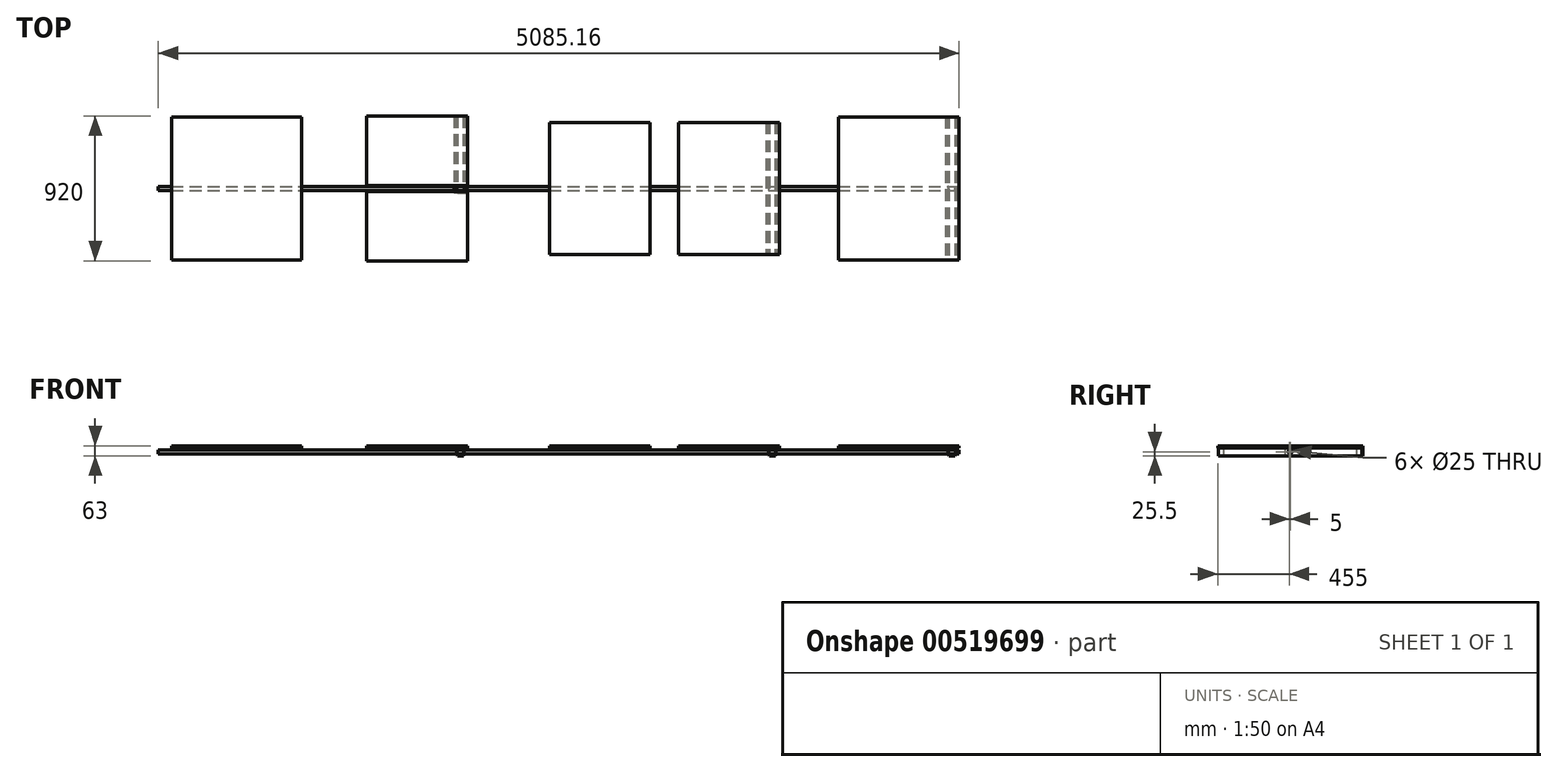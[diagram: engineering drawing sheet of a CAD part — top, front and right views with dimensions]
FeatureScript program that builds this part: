
annotation { "Feature Type Name" : "Feature", "Feature Type Description" : "" }
export const myFeature = defineFeature(function(context is Context, id is Id, definition is map)
    precondition{}
    {
        {
            var Q0;
            Q0=qCreatedBy(makeId("Top.planeOp"),FACE);
            var sketch = newSketch(context, id + "F0", { "sketchPlane" : qUnion([Q0])});
            skLineSegment(sketch, "E0.bottom", {"start": v(-1865.43, 455.05) * mm, "end": v(-2691.93, 455.05) * mm});
            skLineSegment(sketch, "E0.top", {"start": v(-1865.43, -455.05) * mm, "end": v(-2691.93, -455.05) * mm});
            skLineSegment(sketch, "E0.left", {"start": v(-1865.43, 455.05) * mm, "end": v(-1865.43, -455.05) * mm});
            skLineSegment(sketch, "E0.right", {"start": v(-2691.93, 455.05) * mm, "end": v(-2691.93, -455.05) * mm});
            skPoint(sketch, "E0.middle", {"position": v(-2278.68, 0) * mm});
            skLineSegment(sketch, "E1", {"start": v(3394.25, 0) * mm, "end": v(-3825.46, 0) * mm, "construction": true});
            skLineSegment(sketch, "E2", {"start": v(-2691.93, -435.05) * mm, "end": v(-1865.43, -435.05) * mm, "construction": true});
            skLineSegment(sketch, "E3", {"start": v(-2671.93, 455.05) * mm, "end": v(-2671.93, -455.05) * mm, "construction": true});
            skLineSegment(sketch, "E4.0.1.0", {"start": v(-2691.93, -310.75) * mm, "end": v(-1865.43, -310.75) * mm, "construction": true});
            skLineSegment(sketch, "E4.0.2.0", {"start": v(-2691.93, -186.45) * mm, "end": v(-1865.43, -186.45) * mm, "construction": true});
            skLineSegment(sketch, "E4.0.3.0", {"start": v(-2691.93, -62.15) * mm, "end": v(-1865.43, -62.15) * mm, "construction": true});
            skLineSegment(sketch, "E4.0.4.0", {"start": v(-2691.93, 62.15) * mm, "end": v(-1865.43, 62.15) * mm, "construction": true});
            skLineSegment(sketch, "E4.0.5.0", {"start": v(-2691.93, 186.45) * mm, "end": v(-1865.43, 186.45) * mm, "construction": true});
            skLineSegment(sketch, "E4.0.6.0", {"start": v(-2691.93, 310.75) * mm, "end": v(-1865.43, 310.75) * mm, "construction": true});
            skLineSegment(sketch, "E4.0.7.0", {"start": v(-2691.93, 435.05) * mm, "end": v(-1865.43, 435.05) * mm, "construction": true});
            skLineSegment(sketch, "E4.direction1", {"start": v(-2691.93, -435.05) * mm, "end": v(-2691.93, -435.05) * mm});
            skLineSegment(sketch, "E4.direction2", {"start": v(-2691.93, -435.05) * mm, "end": v(-2691.93, -310.75) * mm, "construction": true});
            skLineSegment(sketch, "E5.1.0.0", {"start": v(-2611.43, 455.05) * mm, "end": v(-2611.43, -455.05) * mm, "construction": true});
            skLineSegment(sketch, "E5.2.0.0", {"start": v(-2550.93, 455.05) * mm, "end": v(-2550.93, -455.05) * mm, "construction": true});
            skLineSegment(sketch, "E5.3.0.0", {"start": v(-2490.43, 455.05) * mm, "end": v(-2490.43, -455.05) * mm, "construction": true});
            skLineSegment(sketch, "E5.4.0.0", {"start": v(-2429.93, 455.05) * mm, "end": v(-2429.93, -455.05) * mm, "construction": true});
            skLineSegment(sketch, "E5.5.0.0", {"start": v(-2369.43, 455.05) * mm, "end": v(-2369.43, -455.05) * mm, "construction": true});
            skLineSegment(sketch, "E5.6.0.0", {"start": v(-2308.93, 455.05) * mm, "end": v(-2308.93, -455.05) * mm, "construction": true});
            skLineSegment(sketch, "E5.7.0.0", {"start": v(-2248.43, 455.05) * mm, "end": v(-2248.43, -455.05) * mm, "construction": true});
            skLineSegment(sketch, "E5.8.0.0", {"start": v(-2187.93, 455.05) * mm, "end": v(-2187.93, -455.05) * mm, "construction": true});
            skLineSegment(sketch, "E5.9.0.0", {"start": v(-2127.43, 455.05) * mm, "end": v(-2127.43, -455.05) * mm, "construction": true});
            skLineSegment(sketch, "E5.10.0.0", {"start": v(-2066.93, 455.05) * mm, "end": v(-2066.93, -455.05) * mm, "construction": true});
            skLineSegment(sketch, "E5.11.0.0", {"start": v(-2006.43, 455.05) * mm, "end": v(-2006.43, -455.05) * mm, "construction": true});
            skLineSegment(sketch, "E5.12.0.0", {"start": v(-1945.93, 455.05) * mm, "end": v(-1945.93, -455.05) * mm, "construction": true});
            skLineSegment(sketch, "E5.13.0.0", {"start": v(-1885.43, 455.05) * mm, "end": v(-1885.43, -455.05) * mm, "construction": true});
            skLineSegment(sketch, "E5.direction1", {"start": v(-2671.93, -455.05) * mm, "end": v(-2611.43, -455.05) * mm, "construction": true});
            skLineSegment(sketch, "E6", {"start": v(-2611.43, -310.75) * mm, "end": v(-2611.43, -435.05) * mm, "construction": true});
            skLineSegment(sketch, "E7", {"start": v(-2611.43, -310.75) * mm, "end": v(-2671.93, -310.75) * mm, "construction": true});
            skLineSegment(sketch, "E8.bottom", {"start": v(2308.9, 455.05) * mm, "end": v(1542.9, 455.05) * mm});
            skLineSegment(sketch, "E8.top", {"start": v(2308.9, -455.05) * mm, "end": v(1542.9, -455.05) * mm});
            skLineSegment(sketch, "E8.left", {"start": v(2308.9, 455.05) * mm, "end": v(2308.9, -455.05) * mm});
            skLineSegment(sketch, "E8.right", {"start": v(1542.9, 455.05) * mm, "end": v(1542.9, -455.05) * mm});
            skPoint(sketch, "E8.middle", {"position": v(1925.9, 0) * mm});
            skLineSegment(sketch, "E9", {"start": v(1542.9, -435.05) * mm, "end": v(2308.9, -435.05) * mm, "construction": true});
            skLineSegment(sketch, "E10", {"start": v(1562.9, 455.05) * mm, "end": v(1562.9, -455.05) * mm, "construction": true});
            skLineSegment(sketch, "E11.0.1.0", {"start": v(1542.9, -310.75) * mm, "end": v(2308.9, -310.75) * mm, "construction": true});
            skLineSegment(sketch, "E11.0.2.0", {"start": v(1542.9, -186.45) * mm, "end": v(2308.9, -186.45) * mm, "construction": true});
            skLineSegment(sketch, "E11.0.3.0", {"start": v(1542.9, -62.15) * mm, "end": v(2308.9, -62.15) * mm, "construction": true});
            skLineSegment(sketch, "E11.0.4.0", {"start": v(1542.9, 62.15) * mm, "end": v(2308.9, 62.15) * mm, "construction": true});
            skLineSegment(sketch, "E11.0.5.0", {"start": v(1542.9, 186.45) * mm, "end": v(2308.9, 186.45) * mm, "construction": true});
            skLineSegment(sketch, "E11.0.6.0", {"start": v(1542.9, 310.75) * mm, "end": v(2308.9, 310.75) * mm, "construction": true});
            skLineSegment(sketch, "E11.0.7.0", {"start": v(1542.9, 435.05) * mm, "end": v(2308.9, 435.05) * mm, "construction": true});
            skLineSegment(sketch, "E11.direction1", {"start": v(1542.9, -435.05) * mm, "end": v(1542.9, -435.05) * mm});
            skLineSegment(sketch, "E11.direction2", {"start": v(1542.9, -435.05) * mm, "end": v(1542.9, -310.75) * mm, "construction": true});
            skLineSegment(sketch, "E12.1.0.0", {"start": v(1623.4, 455.05) * mm, "end": v(1623.4, -455.05) * mm, "construction": true});
            skLineSegment(sketch, "E12.2.0.0", {"start": v(1683.9, 455.05) * mm, "end": v(1683.9, -455.05) * mm, "construction": true});
            skLineSegment(sketch, "E12.3.0.0", {"start": v(1744.4, 455.05) * mm, "end": v(1744.4, -455.05) * mm, "construction": true});
            skLineSegment(sketch, "E12.4.0.0", {"start": v(1804.9, 455.05) * mm, "end": v(1804.9, -455.05) * mm, "construction": true});
            skLineSegment(sketch, "E12.5.0.0", {"start": v(1865.4, 455.05) * mm, "end": v(1865.4, -455.05) * mm, "construction": true});
            skLineSegment(sketch, "E12.6.0.0", {"start": v(1925.9, 455.05) * mm, "end": v(1925.9, -455.05) * mm, "construction": true});
            skLineSegment(sketch, "E12.7.0.0", {"start": v(1986.4, 455.05) * mm, "end": v(1986.4, -455.05) * mm, "construction": true});
            skLineSegment(sketch, "E12.8.0.0", {"start": v(2046.9, 455.05) * mm, "end": v(2046.9, -455.05) * mm, "construction": true});
            skLineSegment(sketch, "E12.9.0.0", {"start": v(2107.4, 455.05) * mm, "end": v(2107.4, -455.05) * mm, "construction": true});
            skLineSegment(sketch, "E12.10.0.0", {"start": v(2167.9, 455.05) * mm, "end": v(2167.9, -455.05) * mm, "construction": true});
            skLineSegment(sketch, "E12.11.0.0", {"start": v(2228.4, 455.05) * mm, "end": v(2228.4, -455.05) * mm, "construction": true});
            skLineSegment(sketch, "E12.12.0.0", {"start": v(2288.9, 455.05) * mm, "end": v(2288.9, -455.05) * mm, "construction": true});
            skLineSegment(sketch, "E12.direction1", {"start": v(1562.9, -455.05) * mm, "end": v(1623.4, -455.05) * mm, "construction": true});
            skLineSegment(sketch, "E13", {"start": v(1623.4, -310.75) * mm, "end": v(1623.4, -435.05) * mm, "construction": true});
            skLineSegment(sketch, "E14", {"start": v(1623.4, -310.75) * mm, "end": v(1562.9, -310.75) * mm, "construction": true});
            skLineSegment(sketch, "E15.bottom", {"start": v(1167.87, 420) * mm, "end": v(527.87, 420) * mm});
            skLineSegment(sketch, "E15.top", {"start": v(1167.87, -420) * mm, "end": v(527.87, -420) * mm});
            skLineSegment(sketch, "E15.left", {"start": v(1167.87, 420) * mm, "end": v(1167.87, -420) * mm});
            skLineSegment(sketch, "E15.right", {"start": v(527.87, 420) * mm, "end": v(527.87, -420) * mm});
            skLineSegment(sketch, "E16", {"start": v(527.87, -400) * mm, "end": v(1167.87, -400) * mm, "construction": true});
            skLineSegment(sketch, "E17", {"start": v(547.87, 420) * mm, "end": v(547.87, -420) * mm, "construction": true});
            skLineSegment(sketch, "E18.0.1.0", {"start": v(527.87, -320) * mm, "end": v(1167.87, -320) * mm, "construction": true});
            skLineSegment(sketch, "E18.0.2.0", {"start": v(527.87, -240) * mm, "end": v(1167.87, -240) * mm, "construction": true});
            skLineSegment(sketch, "E18.0.3.0", {"start": v(527.87, -160) * mm, "end": v(1167.87, -160) * mm, "construction": true});
            skLineSegment(sketch, "E18.0.4.0", {"start": v(527.87, -80) * mm, "end": v(1167.87, -80) * mm, "construction": true});
            skLineSegment(sketch, "E18.0.5.0", {"start": v(527.87, 0) * mm, "end": v(1167.87, 0) * mm, "construction": true});
            skLineSegment(sketch, "E18.0.6.0", {"start": v(527.87, 80) * mm, "end": v(1167.87, 80) * mm, "construction": true});
            skLineSegment(sketch, "E18.0.7.0", {"start": v(527.87, 160) * mm, "end": v(1167.87, 160) * mm, "construction": true});
            skLineSegment(sketch, "E18.direction1", {"start": v(527.87, -400) * mm, "end": v(527.87, -400) * mm});
            skLineSegment(sketch, "E18.direction2", {"start": v(527.87, -400) * mm, "end": v(527.87, -320) * mm, "construction": true});
            skLineSegment(sketch, "E19.1.0.0", {"start": v(587.87, 420) * mm, "end": v(587.87, -420) * mm, "construction": true});
            skLineSegment(sketch, "E19.2.0.0", {"start": v(627.87, 420) * mm, "end": v(627.87, -420) * mm, "construction": true});
            skLineSegment(sketch, "E19.3.0.0", {"start": v(667.87, 420) * mm, "end": v(667.87, -420) * mm, "construction": true});
            skLineSegment(sketch, "E19.4.0.0", {"start": v(707.87, 420) * mm, "end": v(707.87, -420) * mm, "construction": true});
            skLineSegment(sketch, "E19.5.0.0", {"start": v(747.87, 420) * mm, "end": v(747.87, -420) * mm, "construction": true});
            skLineSegment(sketch, "E19.6.0.0", {"start": v(787.87, 420) * mm, "end": v(787.87, -420) * mm, "construction": true});
            skLineSegment(sketch, "E19.7.0.0", {"start": v(827.87, 420) * mm, "end": v(827.87, -420) * mm, "construction": true});
            skLineSegment(sketch, "E19.8.0.0", {"start": v(867.87, 420) * mm, "end": v(867.87, -420) * mm, "construction": true});
            skLineSegment(sketch, "E19.9.0.0", {"start": v(907.87, 420) * mm, "end": v(907.87, -420) * mm, "construction": true});
            skLineSegment(sketch, "E19.10.0.0", {"start": v(947.87, 420) * mm, "end": v(947.87, -420) * mm, "construction": true});
            skLineSegment(sketch, "E19.11.0.0", {"start": v(987.87, 420) * mm, "end": v(987.87, -420) * mm, "construction": true});
            skLineSegment(sketch, "E19.12.0.0", {"start": v(1027.87, 420) * mm, "end": v(1027.87, -420) * mm, "construction": true});
            skLineSegment(sketch, "E19.13.0.0", {"start": v(1067.87, 420) * mm, "end": v(1067.87, -420) * mm, "construction": true});
            skLineSegment(sketch, "E19.direction1", {"start": v(547.87, -420) * mm, "end": v(587.87, -420) * mm, "construction": true});
            skLineSegment(sketch, "E20", {"start": v(587.87, -320) * mm, "end": v(587.87, -400) * mm, "construction": true});
            skLineSegment(sketch, "E21.0.14.0", {"start": v(1107.87, 420) * mm, "end": v(1107.87, -420) * mm, "construction": true});
            skLineSegment(sketch, "E21.0.15.0", {"start": v(1147.87, 420) * mm, "end": v(1147.87, -420) * mm, "construction": true});
            skLineSegment(sketch, "E22.0.0.8", {"start": v(527.87, 240) * mm, "end": v(1167.87, 240) * mm, "construction": true});
            skLineSegment(sketch, "E22.0.0.9", {"start": v(527.87, 320) * mm, "end": v(1167.87, 320) * mm, "construction": true});
            skLineSegment(sketch, "E22.0.0.10", {"start": v(527.87, 400) * mm, "end": v(1167.87, 400) * mm, "construction": true});
            skLineSegment(sketch, "E23.bottom", {"start": v(347.86, 420) * mm, "end": v(-292.14, 420) * mm});
            skLineSegment(sketch, "E23.top", {"start": v(347.86, -420) * mm, "end": v(-292.14, -420) * mm});
            skLineSegment(sketch, "E23.left", {"start": v(347.86, 420) * mm, "end": v(347.86, -420) * mm});
            skLineSegment(sketch, "E23.right", {"start": v(-292.14, 420) * mm, "end": v(-292.14, -420) * mm});
            skPoint(sketch, "E23.middle", {"position": v(27.86, 0) * mm});
            skLineSegment(sketch, "E24", {"start": v(-292.14, -400) * mm, "end": v(347.86, -400) * mm, "construction": true});
            skLineSegment(sketch, "E25", {"start": v(-272.14, 420) * mm, "end": v(-272.14, -420) * mm, "construction": true});
            skLineSegment(sketch, "E26.0.1.0", {"start": v(-292.14, -320) * mm, "end": v(347.86, -320) * mm, "construction": true});
            skLineSegment(sketch, "E26.0.2.0", {"start": v(-292.14, -240) * mm, "end": v(347.86, -240) * mm, "construction": true});
            skLineSegment(sketch, "E26.0.3.0", {"start": v(-292.14, -160) * mm, "end": v(347.86, -160) * mm, "construction": true});
            skLineSegment(sketch, "E26.0.4.0", {"start": v(-292.14, -80) * mm, "end": v(347.86, -80) * mm, "construction": true});
            skLineSegment(sketch, "E26.0.5.0", {"start": v(-292.14, 0) * mm, "end": v(347.86, 0) * mm, "construction": true});
            skLineSegment(sketch, "E26.0.6.0", {"start": v(-292.14, 80) * mm, "end": v(347.86, 80) * mm, "construction": true});
            skLineSegment(sketch, "E26.0.7.0", {"start": v(-292.14, 160) * mm, "end": v(347.86, 160) * mm, "construction": true});
            skLineSegment(sketch, "E26.direction1", {"start": v(-292.14, -400) * mm, "end": v(-292.14, -400) * mm});
            skLineSegment(sketch, "E26.direction2", {"start": v(-292.14, -400) * mm, "end": v(-292.14, -320) * mm, "construction": true});
            skLineSegment(sketch, "E27.1.0.0", {"start": v(-232.14, 420) * mm, "end": v(-232.14, -420) * mm, "construction": true});
            skLineSegment(sketch, "E27.2.0.0", {"start": v(-192.14, 420) * mm, "end": v(-192.14, -420) * mm, "construction": true});
            skLineSegment(sketch, "E27.3.0.0", {"start": v(-152.14, 420) * mm, "end": v(-152.14, -420) * mm, "construction": true});
            skLineSegment(sketch, "E27.4.0.0", {"start": v(-112.14, 420) * mm, "end": v(-112.14, -420) * mm, "construction": true});
            skLineSegment(sketch, "E27.5.0.0", {"start": v(-72.14, 420) * mm, "end": v(-72.14, -420) * mm, "construction": true});
            skLineSegment(sketch, "E27.6.0.0", {"start": v(-32.14, 420) * mm, "end": v(-32.14, -420) * mm, "construction": true});
            skLineSegment(sketch, "E27.7.0.0", {"start": v(7.86, 420) * mm, "end": v(7.86, -420) * mm, "construction": true});
            skLineSegment(sketch, "E27.8.0.0", {"start": v(47.86, 420) * mm, "end": v(47.86, -420) * mm, "construction": true});
            skLineSegment(sketch, "E27.9.0.0", {"start": v(87.86, 420) * mm, "end": v(87.86, -420) * mm, "construction": true});
            skLineSegment(sketch, "E27.10.0.0", {"start": v(127.86, 420) * mm, "end": v(127.86, -420) * mm, "construction": true});
            skLineSegment(sketch, "E27.11.0.0", {"start": v(167.86, 420) * mm, "end": v(167.86, -420) * mm, "construction": true});
            skLineSegment(sketch, "E27.12.0.0", {"start": v(207.86, 420) * mm, "end": v(207.86, -420) * mm, "construction": true});
            skLineSegment(sketch, "E27.13.0.0", {"start": v(247.86, 420) * mm, "end": v(247.86, -420) * mm, "construction": true});
            skLineSegment(sketch, "E27.direction1", {"start": v(-272.14, -420) * mm, "end": v(-232.14, -420) * mm, "construction": true});
            skLineSegment(sketch, "E28", {"start": v(-232.14, -320) * mm, "end": v(-232.14, -400) * mm, "construction": true});
            skLineSegment(sketch, "E29.0.14.0", {"start": v(287.86, 420) * mm, "end": v(287.86, -420) * mm, "construction": true});
            skLineSegment(sketch, "E29.0.15.0", {"start": v(327.86, 420) * mm, "end": v(327.86, -420) * mm, "construction": true});
            skLineSegment(sketch, "E30.0.0.8", {"start": v(-292.14, 240) * mm, "end": v(347.86, 240) * mm, "construction": true});
            skLineSegment(sketch, "E30.0.0.9", {"start": v(-292.14, 320) * mm, "end": v(347.86, 320) * mm, "construction": true});
            skLineSegment(sketch, "E30.0.0.10", {"start": v(-292.14, 400) * mm, "end": v(347.86, 400) * mm, "construction": true});
            skLineSegment(sketch, "E31.bottom", {"start": v(-813.38, 460) * mm, "end": v(-1453.38, 460) * mm});
            skLineSegment(sketch, "E31.top", {"start": v(-813.38, 20) * mm, "end": v(-1453.38, 20) * mm});
            skLineSegment(sketch, "E31.left", {"start": v(-813.38, 460) * mm, "end": v(-813.38, 20) * mm});
            skLineSegment(sketch, "E31.right", {"start": v(-1453.38, 460) * mm, "end": v(-1453.38, 20) * mm});
            skPoint(sketch, "E31.middle", {"position": v(-1133.38, 240) * mm});
            skLineSegment(sketch, "E32", {"start": v(-1453.38, 40) * mm, "end": v(-813.38, 40) * mm, "construction": true});
            skLineSegment(sketch, "E33", {"start": v(-1433.38, 460) * mm, "end": v(-1433.38, 20) * mm, "construction": true});
            skLineSegment(sketch, "E34.0.1.0", {"start": v(-1453.38, 120) * mm, "end": v(-813.38, 120) * mm, "construction": true});
            skLineSegment(sketch, "E34.0.2.0", {"start": v(-1453.38, 200) * mm, "end": v(-813.38, 200) * mm, "construction": true});
            skLineSegment(sketch, "E34.0.3.0", {"start": v(-1453.38, 280) * mm, "end": v(-813.38, 280) * mm, "construction": true});
            skLineSegment(sketch, "E34.0.4.0", {"start": v(-1453.38, 360) * mm, "end": v(-813.38, 360) * mm, "construction": true});
            skLineSegment(sketch, "E34.0.5.0", {"start": v(-1453.38, 440) * mm, "end": v(-813.38, 440) * mm, "construction": true});
            skLineSegment(sketch, "E34.direction1", {"start": v(-1453.38, 40) * mm, "end": v(-1453.38, 40) * mm});
            skLineSegment(sketch, "E34.direction2", {"start": v(-1453.38, 40) * mm, "end": v(-1453.38, 120) * mm, "construction": true});
            skLineSegment(sketch, "E35.1.0.0", {"start": v(-1393.38, 460) * mm, "end": v(-1393.38, 20) * mm, "construction": true});
            skLineSegment(sketch, "E35.2.0.0", {"start": v(-1353.38, 460) * mm, "end": v(-1353.38, 20) * mm, "construction": true});
            skLineSegment(sketch, "E35.3.0.0", {"start": v(-1313.38, 460) * mm, "end": v(-1313.38, 20) * mm, "construction": true});
            skLineSegment(sketch, "E35.4.0.0", {"start": v(-1273.38, 460) * mm, "end": v(-1273.38, 20) * mm, "construction": true});
            skLineSegment(sketch, "E35.5.0.0", {"start": v(-1233.38, 460) * mm, "end": v(-1233.38, 20) * mm, "construction": true});
            skLineSegment(sketch, "E35.6.0.0", {"start": v(-1193.38, 460) * mm, "end": v(-1193.38, 20) * mm, "construction": true});
            skLineSegment(sketch, "E35.7.0.0", {"start": v(-1153.38, 460) * mm, "end": v(-1153.38, 20) * mm, "construction": true});
            skLineSegment(sketch, "E35.8.0.0", {"start": v(-1113.38, 460) * mm, "end": v(-1113.38, 20) * mm, "construction": true});
            skLineSegment(sketch, "E35.9.0.0", {"start": v(-1073.38, 460) * mm, "end": v(-1073.38, 20) * mm, "construction": true});
            skLineSegment(sketch, "E35.10.0.0", {"start": v(-1033.38, 460) * mm, "end": v(-1033.38, 20) * mm, "construction": true});
            skLineSegment(sketch, "E35.11.0.0", {"start": v(-993.38, 460) * mm, "end": v(-993.38, 20) * mm, "construction": true});
            skLineSegment(sketch, "E35.12.0.0", {"start": v(-953.38, 460) * mm, "end": v(-953.38, 20) * mm, "construction": true});
            skLineSegment(sketch, "E35.13.0.0", {"start": v(-913.38, 460) * mm, "end": v(-913.38, 20) * mm, "construction": true});
            skLineSegment(sketch, "E35.direction1", {"start": v(-1433.38, 20) * mm, "end": v(-1393.38, 20) * mm, "construction": true});
            skLineSegment(sketch, "E36", {"start": v(-1393.38, 120) * mm, "end": v(-1393.38, 40) * mm, "construction": true});
            skLineSegment(sketch, "E37", {"start": v(-1393.38, 120) * mm, "end": v(-1433.38, 120) * mm, "construction": true});
            skLineSegment(sketch, "E38.0.14.0", {"start": v(-873.38, 460) * mm, "end": v(-873.38, 20) * mm, "construction": true});
            skLineSegment(sketch, "E38.0.15.0", {"start": v(-833.38, 460) * mm, "end": v(-833.38, 20) * mm, "construction": true});
            skLineSegment(sketch, "E39", {"start": v(-1133.38, 240) * mm, "end": v(-1133.38, 0) * mm, "construction": true});
            skLineSegment(sketch, "E40.MirrorCS", {"start": v(-1433.38, -20) * mm, "end": v(-1393.38, -20) * mm, "construction": true});
            skLineSegment(sketch, "E41.MirrorCS", {"start": v(-1393.38, -120) * mm, "end": v(-1433.38, -120) * mm, "construction": true});
            skLineSegment(sketch, "E42.MirrorCS", {"start": v(-1453.38, -40) * mm, "end": v(-1453.38, -120) * mm, "construction": true});
            skLineSegment(sketch, "E43.MirrorCS", {"start": v(-813.38, -460) * mm, "end": v(-813.38, -20) * mm});
            skLineSegment(sketch, "E44.MirrorCS", {"start": v(-1453.38, -40) * mm, "end": v(-813.38, -40) * mm, "construction": true});
            skLineSegment(sketch, "E45.MirrorCS", {"start": v(-1453.38, -460) * mm, "end": v(-1453.38, -20) * mm});
            skLineSegment(sketch, "E46.MirrorCS", {"start": v(-1453.38, -440) * mm, "end": v(-813.38, -440) * mm, "construction": true});
            skLineSegment(sketch, "E47.MirrorCS", {"start": v(-1393.38, -120) * mm, "end": v(-1393.38, -40) * mm, "construction": true});
            skLineSegment(sketch, "E48.MirrorCS", {"start": v(-813.38, -460) * mm, "end": v(-1453.38, -460) * mm});
            skLineSegment(sketch, "E49.MirrorCS", {"start": v(-833.38, -460) * mm, "end": v(-833.38, -20) * mm, "construction": true});
            skLineSegment(sketch, "E50.MirrorCS", {"start": v(-1433.38, -460) * mm, "end": v(-1433.38, -20) * mm, "construction": true});
            skLineSegment(sketch, "E51.MirrorCS", {"start": v(-813.38, -20) * mm, "end": v(-1453.38, -20) * mm});
            skLineSegment(sketch, "E52.MirrorCS", {"start": v(-1453.38, -280) * mm, "end": v(-813.38, -280) * mm, "construction": true});
            skLineSegment(sketch, "E53.MirrorCS", {"start": v(-1273.38, -460) * mm, "end": v(-1273.38, -20) * mm, "construction": true});
            skLineSegment(sketch, "E54.MirrorCS", {"start": v(-1113.38, -460) * mm, "end": v(-1113.38, -20) * mm, "construction": true});
            skLineSegment(sketch, "E55.MirrorCS", {"start": v(-1453.38, -360) * mm, "end": v(-813.38, -360) * mm, "construction": true});
            skLineSegment(sketch, "E56.MirrorCS", {"start": v(-1153.38, -460) * mm, "end": v(-1153.38, -20) * mm, "construction": true});
            skLineSegment(sketch, "E57.MirrorCS", {"start": v(-1453.38, -200) * mm, "end": v(-813.38, -200) * mm, "construction": true});
            skLineSegment(sketch, "E58.MirrorCS", {"start": v(-953.38, -460) * mm, "end": v(-953.38, -20) * mm, "construction": true});
            skLineSegment(sketch, "E59.MirrorCS", {"start": v(-1453.38, -120) * mm, "end": v(-813.38, -120) * mm, "construction": true});
            skLineSegment(sketch, "E60.MirrorCS", {"start": v(-993.38, -460) * mm, "end": v(-993.38, -20) * mm, "construction": true});
            skLineSegment(sketch, "E61.MirrorCS", {"start": v(-1133.38, -240) * mm, "end": v(-1133.38, 0) * mm, "construction": true});
            skLineSegment(sketch, "E62.MirrorCS", {"start": v(-1313.38, -460) * mm, "end": v(-1313.38, -20) * mm, "construction": true});
            skLineSegment(sketch, "E63.MirrorCS", {"start": v(-1353.38, -460) * mm, "end": v(-1353.38, -20) * mm, "construction": true});
            skLineSegment(sketch, "E64.MirrorCS", {"start": v(-1033.38, -460) * mm, "end": v(-1033.38, -20) * mm, "construction": true});
            skPoint(sketch, "E65.MirrorP", {"position": v(-1133.38, -240) * mm});
            skLineSegment(sketch, "E66.MirrorCS", {"start": v(-873.38, -460) * mm, "end": v(-873.38, -20) * mm, "construction": true});
            skLineSegment(sketch, "E67.MirrorCS", {"start": v(-1233.38, -460) * mm, "end": v(-1233.38, -20) * mm, "construction": true});
            skLineSegment(sketch, "E68.MirrorCS", {"start": v(-1393.38, -460) * mm, "end": v(-1393.38, -20) * mm, "construction": true});
            skLineSegment(sketch, "E69.MirrorCS", {"start": v(-1073.38, -460) * mm, "end": v(-1073.38, -20) * mm, "construction": true});
            skLineSegment(sketch, "E70.MirrorCS", {"start": v(-913.38, -460) * mm, "end": v(-913.38, -20) * mm, "construction": true});
            skLineSegment(sketch, "E71.MirrorCS", {"start": v(-1193.38, -460) * mm, "end": v(-1193.38, -20) * mm, "construction": true});
            skSolve(sketch);
        }
        {
            var Q0;
            Q0=makeQuery(id+"F0.imprint","IMPRINT",FACE,{"disambiguationData":[TD([[makeQuery(id+"F0.imprint","IMPRINT",EDGE,{"derivedFrom":sQuery(id+"F0.wireOp",EDGE,"E0.bottom")}),1.0]])]});
            extrude(context, id + "F1", {"entities" : qUnion([Q0]), "depth" : 12 * mm, "offsetDistance" : 25 * mm});
        }
        {
            var Q0;
            Q0=makeQuery(id+"F0.imprint","IMPRINT",FACE,{"disambiguationData":[TD([[makeQuery(id+"F0.imprint","IMPRINT",EDGE,{"derivedFrom":sQuery(id+"F0.wireOp",EDGE,"E23.bottom")}),1.0]])]});
            extrude(context, id + "F2", {"entities" : qUnion([Q0]), "depth" : 12 * mm, "offsetDistance" : 25 * mm});
        }
        {
            var Q0;
            Q0=makeQuery(id+"F0.imprint","IMPRINT",FACE,{"disambiguationData":[TD([[makeQuery(id+"F0.imprint","IMPRINT",EDGE,{"derivedFrom":sQuery(id+"F0.wireOp",EDGE,"E15.bottom")}),1.0]])]});
            extrude(context, id + "F3", {"entities" : qUnion([Q0]), "depth" : 12 * mm, "offsetDistance" : 25 * mm});
        }
        {
            var Q0;
            Q0=makeQuery(id+"F0.imprint","IMPRINT",FACE,{"disambiguationData":[TD([[makeQuery(id+"F0.imprint","IMPRINT",EDGE,{"derivedFrom":sQuery(id+"F0.wireOp",EDGE,"E8.bottom")}),1.0]])]});
            extrude(context, id + "F4", {"entities" : qUnion([Q0]), "depth" : 12 * mm, "offsetDistance" : 25 * mm});
        }
        {
            var Q0;
            Q0=makeQuery(id+"F4.opExtrude","SWEPT_FACE",FACE,{"disambiguationData":[OSD([sQuery(id+"F0.wireOp",EDGE,"E8.left")])]});
            var sketch = newSketch(context, id + "F5", { "sketchPlane" : qUnion([Q0])});
            skPoint(sketch, "E72.oppositeSnap0", {"position": v(455.05, 6) * mm});
            skLineSegment(sketch, "E72.bottom", {"start": v(-455.05, 0) * mm, "end": v(455.05, 0) * mm});
            skLineSegment(sketch, "E72.top", {"start": v(-455.05, -51) * mm, "end": v(455.05, -51) * mm});
            skLineSegment(sketch, "E72.left", {"start": v(-455.05, 0) * mm, "end": v(-455.05, -51) * mm});
            skLineSegment(sketch, "E72.right", {"start": v(455.05, 0) * mm, "end": v(455.05, -51) * mm});
            skCircle(sketch, "E73", {"center": v(0, -25.5) * mm, "radius": 12.5 * mm});
            skPoint(sketch, "E73.centerSnap0", {"position": v(0, 0) * mm});
            skPoint(sketch, "E74", {"position": v(-455.05, -25.5) * mm});
            skSolve(sketch);
        }
        {
            var Q0;
            Q0 = qSketchRegion(id + "F5", true);
            extrude(context, id + "F6", {"entities" : qUnion([Q0]), "oppositeDirection" : true, "depth" : 10 * mm, "offsetDistance" : 25 * mm});
        }
        {
            var Q0;
            Q0=makeQuery(id+"F3.opExtrude","SWEPT_FACE",FACE,{"disambiguationData":[OSD([sQuery(id+"F0.wireOp",EDGE,"E15.left")])]});
            var sketch = newSketch(context, id + "F7", { "sketchPlane" : qUnion([Q0])});
            skLineSegment(sketch, "E75.bottom", {"start": v(-420, 0) * mm, "end": v(420, 0) * mm});
            skLineSegment(sketch, "E75.top", {"start": v(-420, -51) * mm, "end": v(420, -51) * mm});
            skLineSegment(sketch, "E75.left", {"start": v(-420, 0) * mm, "end": v(-420, -51) * mm});
            skLineSegment(sketch, "E75.right", {"start": v(420, 0) * mm, "end": v(420, -51) * mm});
            skCircle(sketch, "E76", {"center": v(0, -25.5) * mm, "radius": 12.5 * mm});
            skPoint(sketch, "E76.centerSnap0", {"position": v(0, 0) * mm});
            skPoint(sketch, "E77", {"position": v(-420, -25.5) * mm});
            skSolve(sketch);
        }
        {
            var Q0;
            Q0 = qSketchRegion(id + "F7", true);
            extrude(context, id + "F8", {"entities" : qUnion([Q0]), "oppositeDirection" : true, "depth" : 10 * mm, "offsetDistance" : 25 * mm});
        }
        {
            var Q0;
            Q0=makeQuery(id+"F0.imprint","IMPRINT",FACE,{"disambiguationData":[TD([[makeQuery(id+"F0.imprint","IMPRINT",EDGE,{"derivedFrom":sQuery(id+"F0.wireOp",EDGE,"E31.bottom")}),1.0]])]});
            extrude(context, id + "F9", {"entities" : qUnion([Q0]), "depth" : 12 * mm, "offsetDistance" : 25 * mm});
        }
        {
            var Q0;
            Q0=makeQuery(id+"F0.imprint","IMPRINT",FACE,{"disambiguationData":[TD([[makeQuery(id+"F0.imprint","IMPRINT",EDGE,{"derivedFrom":sQuery(id+"F0.wireOp",EDGE,"E43.MirrorCS")}),1.0]])]});
            extrude(context, id + "F10", {"entities" : qUnion([Q0]), "depth" : 12 * mm, "offsetDistance" : 25 * mm});
        }
        {
            var Q0;
            Q0=makeQuery(id+"F9.opExtrude","SWEPT_FACE",FACE,{"disambiguationData":[OSD([sQuery(id+"F0.wireOp",EDGE,"E31.left")])]});
            var sketch = newSketch(context, id + "F11", { "sketchPlane" : qUnion([Q0])});
            skCircle(sketch, "E78.0", {"center": v(-5, -25.5) * mm, "radius": 12.5 * mm});
            skLineSegment(sketch, "E79.bottom", {"start": v(20, 0) * mm, "end": v(460, 0) * mm});
            skLineSegment(sketch, "E79.top", {"start": v(20, -51) * mm, "end": v(460, -51) * mm});
            skLineSegment(sketch, "E79.left", {"start": v(20, 0) * mm, "end": v(20, -51) * mm});
            skLineSegment(sketch, "E79.right", {"start": v(460, 0) * mm, "end": v(460, -51) * mm});
            skLineSegment(sketch, "E80.bottom", {"start": v(20, 0) * mm, "end": v(-30, 0) * mm});
            skLineSegment(sketch, "E80.top", {"start": v(20, -51) * mm, "end": v(-30, -51) * mm});
            skLineSegment(sketch, "E80.right", {"start": v(-30, 0) * mm, "end": v(-30, -51) * mm});
            skPoint(sketch, "E81.0", {"position": v(-30, 0) * mm});
            skPoint(sketch, "E82", {"position": v(-30, -25.5) * mm});
            skPoint(sketch, "E83", {"position": v(-5, 0) * mm});
            skSolve(sketch);
        }
        {
            var Q0;
            Q0 = qSketchRegion(id + "F11", true);
            extrude(context, id + "F12", {"entities" : qUnion([Q0]), "oppositeDirection" : true, "depth" : 10 * mm, "offsetDistance" : 25 * mm});
        }
        {
            var Q0;
            Q0=makeQuery(id+"F12.opExtrude","SWEPT_FACE",FACE,{"disambiguationData":[OSD([sQuery(id+"F11.wireOp",EDGE,"E80.right")])]});
            var sketch = newSketch(context, id + "F13", { "sketchPlane" : qUnion([Q0])});
            skLineSegment(sketch, "E84", {"start": v(-836.32, -50) * mm, "end": v(-845.14, 0) * mm});
            skPoint(sketch, "E85", {"position": v(-818.38, 0) * mm});
            skPoint(sketch, "E86", {"position": v(-818.38, -51) * mm});
            skLineSegment(sketch, "E87", {"start": v(-818.38, -51) * mm, "end": v(-818.38, 0) * mm, "construction": true});
            skLineSegment(sketch, "E88", {"start": v(-845.14, 0) * mm, "end": v(-860.14, 0) * mm});
            skLineSegment(sketch, "E89.MirrorCS", {"start": v(-791.61, 0) * mm, "end": v(-776.61, 0) * mm});
            skLineSegment(sketch, "E90.MirrorCS", {"start": v(-800.43, -50) * mm, "end": v(-791.61, 0) * mm});
            skLineSegment(sketch, "E91", {"start": v(-836.32, -50) * mm, "end": v(-800.43, -50) * mm});
            skLineSegment(sketch, "E92.0", {"start": v(-845.98, -1) * mm, "end": v(-860.14, -1) * mm});
            skLineSegment(sketch, "E92.1", {"start": v(-790.78, -1) * mm, "end": v(-776.61, -1) * mm});
            skLineSegment(sketch, "E92.2", {"start": v(-799.6, -51) * mm, "end": v(-790.78, -1) * mm});
            skLineSegment(sketch, "E92.3", {"start": v(-837.16, -51) * mm, "end": v(-799.6, -51) * mm});
            skLineSegment(sketch, "E92.4", {"start": v(-837.16, -51) * mm, "end": v(-845.98, -1) * mm});
            skLineSegment(sketch, "E93", {"start": v(-860.14, 0) * mm, "end": v(-860.14, -1) * mm});
            skLineSegment(sketch, "E94", {"start": v(-776.61, 0) * mm, "end": v(-776.61, -1) * mm});
            skSolve(sketch);
        }
        {
            var Q0;
            Q0 = qSketchRegion(id + "F13", true);
            var Q1;
            Q1=makeQuery(id+"F12.opExtrude","SWEPT_FACE",FACE,{"disambiguationData":[OSD([sQuery(id+"F11.wireOp",EDGE,"E79.right")])]});
            extrude(context, id + "F14", {"entities" : qUnion([Q0]), "endBound" : BoundingType.UP_TO_SURFACE, "oppositeDirection" : true, "depth" : 25 * mm, "endBoundEntityFace" : qUnion([Q1]), "offsetDistance" : 25 * mm});
        }
        {
            var Q0;
            Q0=makeQuery(id+"F14.opExtrude","SWEPT_FACE",FACE,{"disambiguationData":[OSD([sQuery(id+"F13.wireOp",EDGE,"E94")])]});
            var sketch = newSketch(context, id + "F15", { "sketchPlane" : qUnion([Q0])});
            skCircle(sketch, "E95.0", {"center": v(-5, -25.5) * mm, "radius": 12.5 * mm});
            skLineSegment(sketch, "E96.0.0", {"start": v(460, -51) * mm, "end": v(460, -1) * mm});
            skLineSegment(sketch, "E96.0.1", {"start": v(460, -1) * mm, "end": v(-30, -1) * mm});
            skLineSegment(sketch, "E96.0.2", {"start": v(-30, -1) * mm, "end": v(-30, -51) * mm});
            skLineSegment(sketch, "E96.0.3", {"start": v(-30, -51) * mm, "end": v(460, -51) * mm});
            skSolve(sketch);
        }
        {
            var Q0;
            Q0=makeQuery(id+"F15.imprint","IMPRINT",FACE,{"disambiguationData":[TD([[makeQuery(id+"F15.imprint","IMPRINT",EDGE,{"derivedFrom":sQuery(id+"F15.wireOp",EDGE,"E95.0")}),1.0]])]});
            var Q1;
            Q1=sQuery(id+"F15.wireOp",EDGE,"E95.0");
            var Q2;
            Q2=makeQuery(id+"F14.opExtrude","SWEPT_FACE",FACE,{"disambiguationData":[OSD([sQuery(id+"F13.wireOp",EDGE,"E92.4")])]});
            extrude(context, id + "F16", {"entities" : qUnion([Q0]), "operationType" : NewBodyOperationType.REMOVE, "surfaceEntities" : qUnion([Q1]), "endBound" : BoundingType.UP_TO_SURFACE, "oppositeDirection" : true, "depth" : 25 * mm, "endBoundEntityFace" : qUnion([Q2]), "offsetDistance" : 25 * mm});
        }
        {
            var Q0;
            Q0=makeQuery(id+"F3.opExtrude","SWEPT_FACE",FACE,{"disambiguationData":[OSD([sQuery(id+"F0.wireOp",EDGE,"E15.top")])]});
            var sketch = newSketch(context, id + "F17", { "sketchPlane" : qUnion([Q0])});
            skLineSegment(sketch, "E97", {"start": v(1144.92, -50) * mm, "end": v(1136.1, 0) * mm});
            skPoint(sketch, "E98", {"position": v(1162.87, -9.43) * mm});
            skPoint(sketch, "E99", {"position": v(1162.87, -51) * mm});
            skLineSegment(sketch, "E100", {"start": v(1162.87, -51) * mm, "end": v(1162.87, -9.43) * mm, "construction": true});
            skLineSegment(sketch, "E101", {"start": v(1136.1, 0) * mm, "end": v(1121.1, 0) * mm});
            skLineSegment(sketch, "E102.MirrorCS", {"start": v(1189.63, 0) * mm, "end": v(1204.63, 0) * mm});
            skLineSegment(sketch, "E103.MirrorCS", {"start": v(1180.81, -50) * mm, "end": v(1189.63, 0) * mm});
            skLineSegment(sketch, "E104", {"start": v(1144.92, -50) * mm, "end": v(1180.81, -50) * mm});
            skLineSegment(sketch, "E105.0", {"start": v(1135.27, -1) * mm, "end": v(1121.1, -1) * mm});
            skLineSegment(sketch, "E105.1", {"start": v(1190.47, -1) * mm, "end": v(1204.63, -1) * mm});
            skLineSegment(sketch, "E105.2", {"start": v(1181.65, -51) * mm, "end": v(1190.47, -1) * mm});
            skLineSegment(sketch, "E105.3", {"start": v(1144.08, -51) * mm, "end": v(1181.65, -51) * mm});
            skLineSegment(sketch, "E105.4", {"start": v(1144.08, -51) * mm, "end": v(1135.27, -1) * mm});
            skLineSegment(sketch, "E106", {"start": v(1121.1, 0) * mm, "end": v(1121.1, -1) * mm});
            skLineSegment(sketch, "E107", {"start": v(1204.63, 0) * mm, "end": v(1204.63, -1) * mm});
            skLineSegment(sketch, "E108.0", {"start": v(1167.87, 0) * mm, "end": v(527.87, 0) * mm});
            skSolve(sketch);
        }
        {
            var Q0;
            Q0 = qSketchRegion(id + "F17", true);
            var Q1;
            Q1=makeQuery(id+"F3.opExtrude","SWEPT_FACE",FACE,{"disambiguationData":[OSD([sQuery(id+"F0.wireOp",EDGE,"E15.bottom")])]});
            extrude(context, id + "F18", {"entities" : qUnion([Q0]), "endBound" : BoundingType.UP_TO_SURFACE, "oppositeDirection" : true, "depth" : 25 * mm, "endBoundEntityFace" : qUnion([Q1]), "offsetDistance" : 25 * mm});
        }
        {
            var Q0;
            Q0=makeQuery(id+"F18.opExtrude","SWEPT_FACE",FACE,{"disambiguationData":[OSD([sQuery(id+"F17.wireOp",EDGE,"E107")])]});
            var sketch = newSketch(context, id + "F19", { "sketchPlane" : qUnion([Q0])});
            skLineSegment(sketch, "E109.0.0", {"start": v(420, -51) * mm, "end": v(420, -1) * mm});
            skLineSegment(sketch, "E109.0.1", {"start": v(420, -1) * mm, "end": v(-420, -1) * mm});
            skLineSegment(sketch, "E109.0.2", {"start": v(-420, -1) * mm, "end": v(-420, -51) * mm});
            skLineSegment(sketch, "E109.0.3", {"start": v(-420, -51) * mm, "end": v(420, -51) * mm});
            skCircle(sketch, "E110", {"center": v(0, -25.5) * mm, "radius": 12.5 * mm});
            skPoint(sketch, "E110.centerSnap0", {"position": v(420, -26) * mm});
            skPoint(sketch, "E111", {"position": v(0, -1) * mm});
            skSolve(sketch);
        }
        {
            var Q0;
            Q0=makeQuery(id+"F19.imprint","IMPRINT",FACE,{"disambiguationData":[TD([[makeQuery(id+"F19.imprint","IMPRINT",EDGE,{"derivedFrom":sQuery(id+"F19.wireOp",EDGE,"E110")}),1.0]])]});
            var Q1;
            Q1=makeQuery(id+"F18.opExtrude","SWEPT_FACE",FACE,{"disambiguationData":[OSD([sQuery(id+"F17.wireOp",EDGE,"E105.4")])]});
            extrude(context, id + "F20", {"entities" : qUnion([Q0]), "operationType" : NewBodyOperationType.REMOVE, "endBound" : BoundingType.UP_TO_SURFACE, "oppositeDirection" : true, "depth" : 25 * mm, "endBoundEntityFace" : qUnion([Q1]), "offsetDistance" : 25 * mm});
        }
        {
            var Q0;
            Q0=makeQuery(id+"F4.opExtrude","SWEPT_FACE",FACE,{"disambiguationData":[OSD([sQuery(id+"F0.wireOp",EDGE,"E8.top")])]});
            var sketch = newSketch(context, id + "F21", { "sketchPlane" : qUnion([Q0])});
            skLineSegment(sketch, "E112", {"start": v(2285.96, -50) * mm, "end": v(2277.15, 0) * mm});
            skPoint(sketch, "E113", {"position": v(2303.9, -9.43) * mm});
            skPoint(sketch, "E114", {"position": v(2303.9, -51) * mm});
            skLineSegment(sketch, "E115", {"start": v(2303.9, -51) * mm, "end": v(2303.9, -9.43) * mm, "construction": true});
            skLineSegment(sketch, "E116", {"start": v(2277.15, 0) * mm, "end": v(2262.15, 0) * mm});
            skLineSegment(sketch, "E117.MirrorCS", {"start": v(2330.67, 0) * mm, "end": v(2345.67, 0) * mm});
            skLineSegment(sketch, "E118.MirrorCS", {"start": v(2321.86, -50) * mm, "end": v(2330.67, 0) * mm});
            skLineSegment(sketch, "E119", {"start": v(2285.96, -50) * mm, "end": v(2321.86, -50) * mm});
            skLineSegment(sketch, "E120.0", {"start": v(2276.3, -1) * mm, "end": v(2262.15, -1) * mm});
            skLineSegment(sketch, "E120.1", {"start": v(2331.51, -1) * mm, "end": v(2345.67, -1) * mm});
            skLineSegment(sketch, "E120.2", {"start": v(2322.7, -51) * mm, "end": v(2331.51, -1) * mm});
            skLineSegment(sketch, "E120.3", {"start": v(2285.12, -51) * mm, "end": v(2322.7, -51) * mm});
            skLineSegment(sketch, "E120.4", {"start": v(2285.12, -51) * mm, "end": v(2276.3, -1) * mm});
            skLineSegment(sketch, "E121", {"start": v(2262.15, 0) * mm, "end": v(2262.15, -1) * mm});
            skLineSegment(sketch, "E122", {"start": v(2345.67, 0) * mm, "end": v(2345.67, -1) * mm});
            skLineSegment(sketch, "E123.0", {"start": v(2328.4, 0) * mm, "end": v(1688.4, 0) * mm});
            skSolve(sketch);
        }
        {
            var Q0;
            Q0 = qSketchRegion(id + "F21", true);
            var Q1;
            Q1=makeQuery(id+"F4.opExtrude","SWEPT_FACE",FACE,{"disambiguationData":[OSD([sQuery(id+"F0.wireOp",EDGE,"E8.bottom")])]});
            extrude(context, id + "F22", {"entities" : qUnion([Q0]), "endBound" : BoundingType.UP_TO_SURFACE, "oppositeDirection" : true, "depth" : 25 * mm, "endBoundEntityFace" : qUnion([Q1]), "offsetDistance" : 25 * mm});
        }
        {
            var Q0;
            Q0=makeQuery(id+"F22.opExtrude","SWEPT_FACE",FACE,{"disambiguationData":[OSD([sQuery(id+"F21.wireOp",EDGE,"E122")])]});
            var sketch = newSketch(context, id + "F23", { "sketchPlane" : qUnion([Q0])});
            skLineSegment(sketch, "E124.0.0", {"start": v(455.05, -51) * mm, "end": v(455.05, -1) * mm});
            skLineSegment(sketch, "E124.0.1", {"start": v(455.05, -1) * mm, "end": v(-455.05, -1) * mm});
            skLineSegment(sketch, "E124.0.2", {"start": v(-455.05, -1) * mm, "end": v(-455.05, -51) * mm});
            skLineSegment(sketch, "E124.0.3", {"start": v(-455.05, -51) * mm, "end": v(455.05, -51) * mm});
            skCircle(sketch, "E125", {"center": v(0, -25.5) * mm, "radius": 12.5 * mm});
            skPoint(sketch, "E125.centerSnap0", {"position": v(455.05, -26) * mm});
            skPoint(sketch, "E126", {"position": v(0, -1) * mm});
            skSolve(sketch);
        }
        {
            var Q0;
            Q0=makeQuery(id+"F23.imprint","IMPRINT",FACE,{"disambiguationData":[TD([[makeQuery(id+"F23.imprint","IMPRINT",EDGE,{"derivedFrom":sQuery(id+"F23.wireOp",EDGE,"E125")}),1.0]])]});
            var Q1;
            Q1=makeQuery(id+"F22.opExtrude","SWEPT_FACE",FACE,{"disambiguationData":[OSD([sQuery(id+"F21.wireOp",EDGE,"E120.4")])]});
            extrude(context, id + "F24", {"entities" : qUnion([Q0]), "operationType" : NewBodyOperationType.REMOVE, "endBound" : BoundingType.UP_TO_SURFACE, "oppositeDirection" : true, "depth" : 25 * mm, "endBoundEntityFace" : qUnion([Q1]), "offsetDistance" : 25 * mm});
        }
        {
            var Q0;
            Q0=makeQuery(id+"F14.opExtrude","SWEPT_BODY",BODY,{"disambiguationData":[OSD([sQuery(id+"F13.wireOp",EDGE,"E84"),sQuery(id+"F13.wireOp",EDGE,"E88"),sQuery(id+"F13.wireOp",EDGE,"E89.MirrorCS"),sQuery(id+"F13.wireOp",EDGE,"E90.MirrorCS"),sQuery(id+"F13.wireOp",EDGE,"E91"),sQuery(id+"F13.wireOp",EDGE,"E92.0"),sQuery(id+"F13.wireOp",EDGE,"E92.1"),sQuery(id+"F13.wireOp",EDGE,"E92.2"),sQuery(id+"F13.wireOp",EDGE,"E92.3"),sQuery(id+"F13.wireOp",EDGE,"E92.4"),sQuery(id+"F13.wireOp",EDGE,"E93"),sQuery(id+"F13.wireOp",EDGE,"E94")])]});
            var Q1;
            Q1=makeQuery(id+"F18.opExtrude","SWEPT_BODY",BODY,{"disambiguationData":[OSD([sQuery(id+"F17.wireOp",EDGE,"E97"),sQuery(id+"F17.wireOp",EDGE,"E102.MirrorCS"),sQuery(id+"F17.wireOp",EDGE,"E103.MirrorCS"),sQuery(id+"F17.wireOp",EDGE,"E104"),sQuery(id+"F17.wireOp",EDGE,"E105.0"),sQuery(id+"F17.wireOp",EDGE,"E105.1"),sQuery(id+"F17.wireOp",EDGE,"E105.2"),sQuery(id+"F17.wireOp",EDGE,"E105.3"),sQuery(id+"F17.wireOp",EDGE,"E105.4"),sQuery(id+"F17.wireOp",EDGE,"E106"),sQuery(id+"F17.wireOp",EDGE,"E107"),sQuery(id+"F17.wireOp",EDGE,"E108.0")])]});
            var Q2;
            Q2=makeQuery(id+"F22.opExtrude","SWEPT_BODY",BODY,{"disambiguationData":[OSD([sQuery(id+"F21.wireOp",EDGE,"E112"),sQuery(id+"F21.wireOp",EDGE,"E117.MirrorCS"),sQuery(id+"F21.wireOp",EDGE,"E118.MirrorCS"),sQuery(id+"F21.wireOp",EDGE,"E119"),sQuery(id+"F21.wireOp",EDGE,"E120.0"),sQuery(id+"F21.wireOp",EDGE,"E120.1"),sQuery(id+"F21.wireOp",EDGE,"E120.2"),sQuery(id+"F21.wireOp",EDGE,"E120.3"),sQuery(id+"F21.wireOp",EDGE,"E120.4"),sQuery(id+"F21.wireOp",EDGE,"E121"),sQuery(id+"F21.wireOp",EDGE,"E122"),sQuery(id+"F21.wireOp",EDGE,"E123.0")])]});
            transform(context, id + "F25", {"entities" : qUnion([Q0, Q1, Q2]), "transformType" : TransformType.TRANSLATION_3D, "dx" : -39 * mm, "dy" : 0 * mm, "dz" : 0 * mm, "makeCopy" : false});
        }
        {
            var Q0;
            Q0=makeQuery(id+"F8.opExtrude","SWEPT_BODY",BODY,{"disambiguationData":[OSD([sQuery(id+"F7.wireOp",EDGE,"E75.bottom"),sQuery(id+"F7.wireOp",EDGE,"E75.top"),sQuery(id+"F7.wireOp",EDGE,"E75.left"),sQuery(id+"F7.wireOp",EDGE,"E75.right"),sQuery(id+"F7.wireOp",EDGE,"E76")])]});
            var Q1;
            Q1=makeQuery(id+"F12.opExtrude","SWEPT_BODY",BODY,{"disambiguationData":[OSD([sQuery(id+"F11.wireOp",EDGE,"E78.0"),sQuery(id+"F11.wireOp",EDGE,"E79.bottom"),sQuery(id+"F11.wireOp",EDGE,"E79.top"),sQuery(id+"F11.wireOp",EDGE,"E79.right"),sQuery(id+"F11.wireOp",EDGE,"E80.bottom"),sQuery(id+"F11.wireOp",EDGE,"E80.top"),sQuery(id+"F11.wireOp",EDGE,"E80.right")])]});
            var Q2;
            Q2=makeQuery(id+"F6.opExtrude","SWEPT_BODY",BODY,{"disambiguationData":[OSD([sQuery(id+"F5.wireOp",EDGE,"E72.bottom"),sQuery(id+"F5.wireOp",EDGE,"E72.top"),sQuery(id+"F5.wireOp",EDGE,"E72.left"),sQuery(id+"F5.wireOp",EDGE,"E72.right"),sQuery(id+"F5.wireOp",EDGE,"E73")])]});
            deleteBodies(context, id + "F26", {"entities" : qUnion([Q0, Q1, Q2])});
        }
        {
            var Q0;
            Q0=makeQuery(id+"F4.opExtrude","SWEPT_FACE",FACE,{"disambiguationData":[OSD([sQuery(id+"F0.wireOp",EDGE,"E8.left")])]});
            var sketch = newSketch(context, id + "F27", { "sketchPlane" : qUnion([Q0])});
            skCircle(sketch, "E127.0", {"center": v(0, -25.5) * mm, "radius": 12.5 * mm});
            skSolve(sketch);
        }
        {
            var Q0;
            Q0=makeQuery(id+"F27.imprint","IMPRINT",FACE,{"disambiguationData":[TD([[makeQuery(id+"F27.imprint","IMPRINT",EDGE,{"derivedFrom":sQuery(id+"F27.wireOp",EDGE,"E127.0")}),1.0]])]});
            extrude(context, id + "F28", {"entities" : qUnion([Q0]), "endBound" : BoundingType.THROUGH_ALL, "oppositeDirection" : true, "depth" : 25 * mm, "offsetDistance" : 25 * mm});
        }
    });
